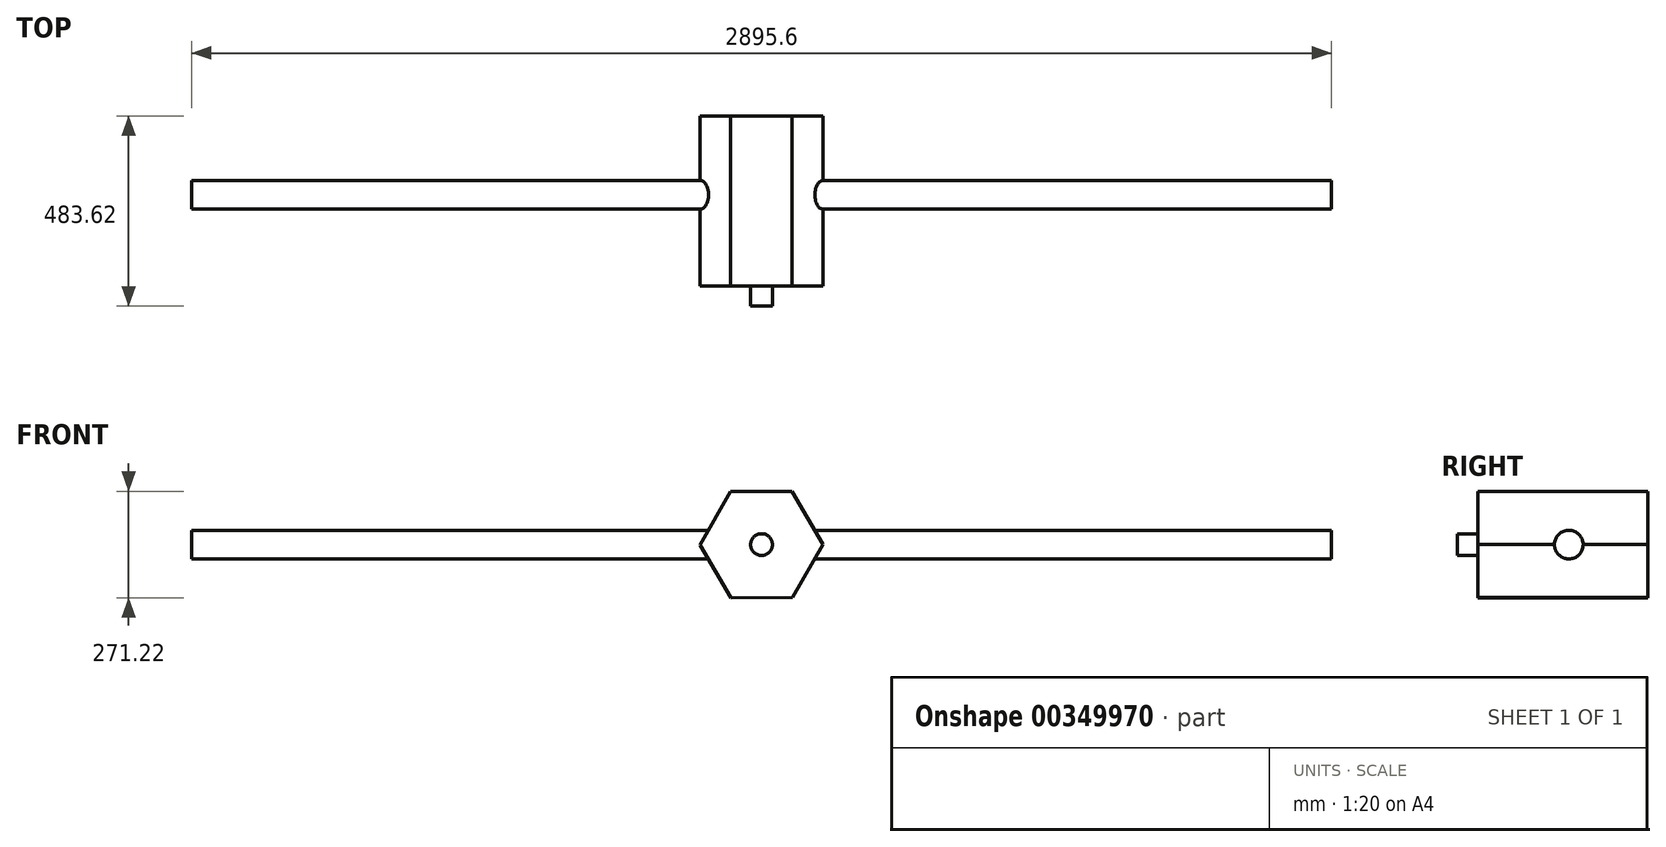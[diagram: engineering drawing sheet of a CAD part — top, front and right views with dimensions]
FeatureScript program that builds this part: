
annotation { "Feature Type Name" : "Feature", "Feature Type Description" : "" }
export const myFeature = defineFeature(function(context is Context, id is Id, definition is map)
    precondition{}
    {
        {
            var Q0;
            Q0=qCreatedBy(makeId("Front.planeOp"),FACE);
            var sketch = newSketch(context, id + "F0", { "sketchPlane" : qUnion([Q0])});
            skCircle(sketch, "E0.cCircle", {"center": v(0, 0) * mm, "radius": 135.2 * mm, "construction": true});
            skLineSegment(sketch, "E0.0", {"start": v(156.12, 0.81) * mm, "end": v(78.77, -134.8) * mm});
            skLineSegment(sketch, "E0.1", {"start": v(78.77, -134.8) * mm, "end": v(-77.36, -135.61) * mm});
            skLineSegment(sketch, "E0.2", {"start": v(-77.36, -135.61) * mm, "end": v(-156.12, -0.81) * mm});
            skLineSegment(sketch, "E0.3", {"start": v(-156.12, -0.81) * mm, "end": v(-78.77, 134.8) * mm});
            skLineSegment(sketch, "E0.4", {"start": v(-78.77, 134.8) * mm, "end": v(77.36, 135.61) * mm});
            skLineSegment(sketch, "E0.5", {"start": v(77.36, 135.61) * mm, "end": v(156.12, 0.81) * mm});
            skPoint(sketch, "E0.0.midPoint", {"position": v(117.44, -67) * mm});
            skSolve(sketch);
        }
        {
            var Q0;
            Q0 = qSketchRegion(id + "F0", true);
            extrude(context, id + "F1", {"entities" : qUnion([Q0]), "depth" : 431.8 * mm});
        }
        {
            var Q0;
            Q0=makeQuery(id+"F1.opExtrude","CAP_FACE",FACE,{"disambiguationData":[OSD([sQuery(id+"F0.wireOp",EDGE,"E0.0"),sQuery(id+"F0.wireOp",EDGE,"E0.1"),sQuery(id+"F0.wireOp",EDGE,"E0.2"),sQuery(id+"F0.wireOp",EDGE,"E0.3"),sQuery(id+"F0.wireOp",EDGE,"E0.4"),sQuery(id+"F0.wireOp",EDGE,"E0.5")])],"isStart":false});
            var sketch = newSketch(context, id + "F2", { "sketchPlane" : qUnion([Q0])});
            skCircle(sketch, "E1", {"center": v(0, 0) * mm, "radius": 27.74 * mm});
            skSolve(sketch);
        }
        {
            var Q0;
            Q0 = qSketchRegion(id + "F2", true);
            extrude(context, id + "F3", {"entities" : qUnion([Q0]), "operationType" : NewBodyOperationType.ADD, "depth" : 51.82 * mm});
        }
        {
            var Q0;
            Q0=qCreatedBy(makeId("Right.planeOp"),FACE);
            var sketch = newSketch(context, id + "F4", { "sketchPlane" : qUnion([Q0])});
            skCircle(sketch, "E2", {"center": v(-200.55, 0) * mm, "radius": 36.46 * mm});
            skSolve(sketch);
        }
        {
            var Q0;
            Q0 = qSketchRegion(id + "F4", true);
            extrude(context, id + "F5", {"entities" : qUnion([Q0]), "operationType" : NewBodyOperationType.ADD, "endBound" : BoundingType.SYMMETRIC, "depth" : 2895.6 * mm, "offsetDistance" : 25.4 * mm});
        }
    });
